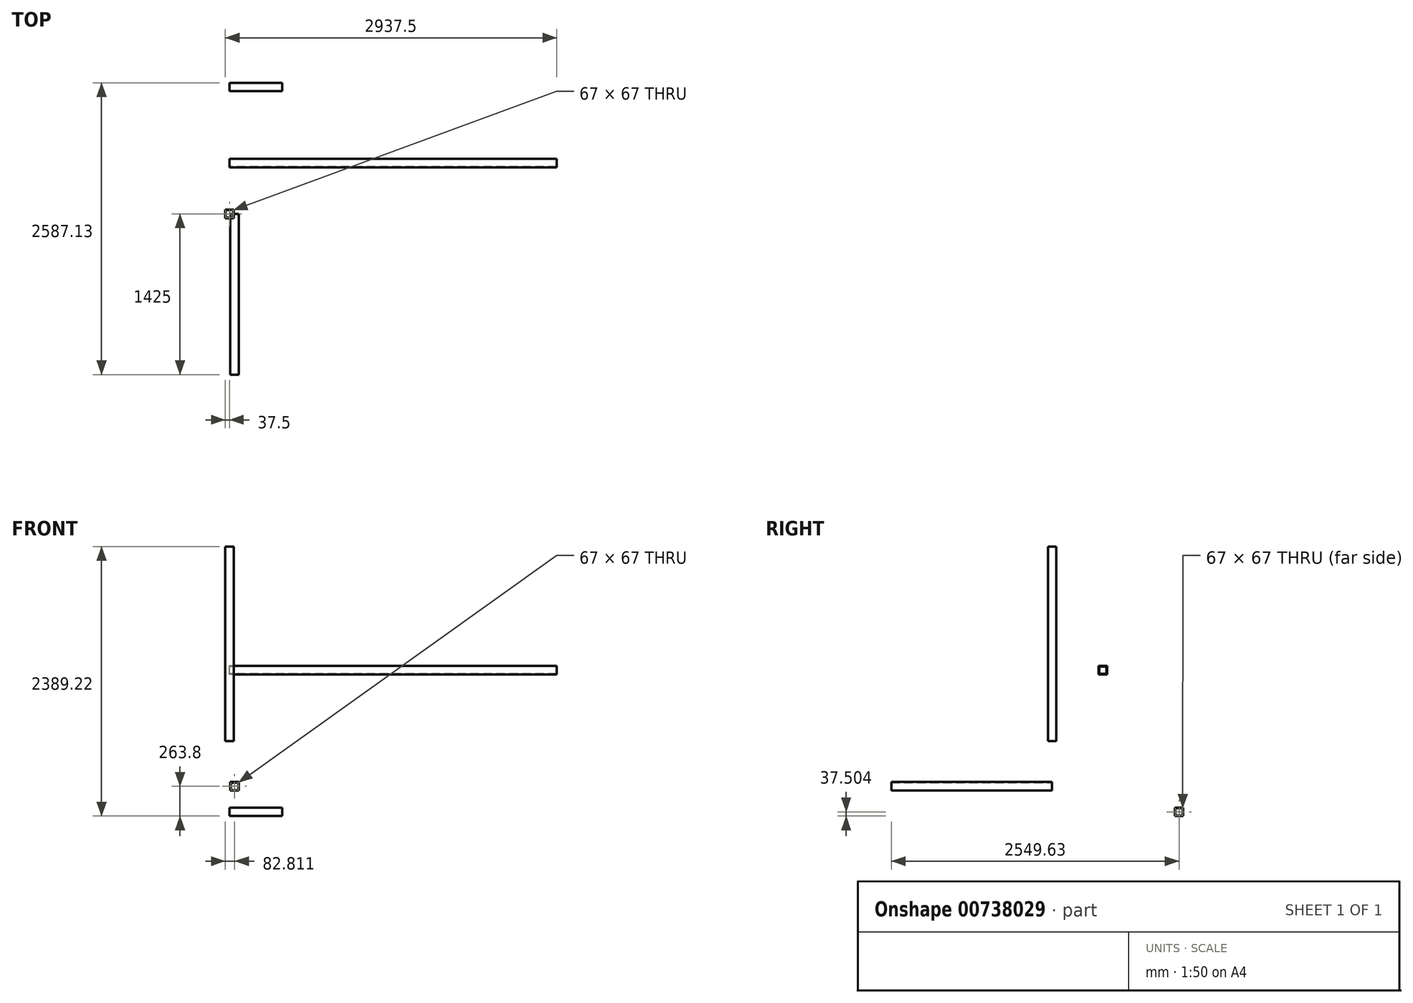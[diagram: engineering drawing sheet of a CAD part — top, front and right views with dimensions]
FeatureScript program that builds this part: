
annotation { "Feature Type Name" : "Feature", "Feature Type Description" : "" }
export const myFeature = defineFeature(function(context is Context, id is Id, definition is map)
    precondition{}
    {
        {
            var Q0;
            Q0=qCreatedBy(makeId("Top.planeOp"),FACE);
            var sketch = newSketch(context, id + "F0", { "sketchPlane" : qUnion([Q0])});
            skLineSegment(sketch, "E0.bottom", {"start": v(37.5, -37.5) * mm, "end": v(-37.5, -37.5) * mm});
            skLineSegment(sketch, "E0.top", {"start": v(37.5, 37.5) * mm, "end": v(-37.5, 37.5) * mm});
            skLineSegment(sketch, "E0.left", {"start": v(37.5, -37.5) * mm, "end": v(37.5, 37.5) * mm});
            skLineSegment(sketch, "E0.right", {"start": v(-37.5, -37.5) * mm, "end": v(-37.5, 37.5) * mm});
            skPoint(sketch, "E0.middle", {"position": v(0, 0) * mm});
            skLineSegment(sketch, "E1.0", {"start": v(33.5, 33.5) * mm, "end": v(-33.5, 33.5) * mm});
            skLineSegment(sketch, "E1.1", {"start": v(33.5, -33.5) * mm, "end": v(33.5, 33.5) * mm});
            skLineSegment(sketch, "E1.2", {"start": v(33.5, -33.5) * mm, "end": v(-33.5, -33.5) * mm});
            skLineSegment(sketch, "E1.3", {"start": v(-33.5, -33.5) * mm, "end": v(-33.5, 33.5) * mm});
            skLineSegment(sketch, "E2.bottom", {"start": v(-2581.2, 0) * mm, "end": v(-2506.2, 0) * mm});
            skLineSegment(sketch, "E2.top", {"start": v(-2581.2, -75) * mm, "end": v(-2506.2, -75) * mm});
            skLineSegment(sketch, "E2.left", {"start": v(-2581.2, 0) * mm, "end": v(-2581.2, -75) * mm});
            skLineSegment(sketch, "E2.right", {"start": v(-2506.2, 0) * mm, "end": v(-2506.2, -75) * mm});
            skPoint(sketch, "E2.middle", {"position": v(-2543.7, -37.5) * mm});
            skLineSegment(sketch, "E3.0", {"start": v(-2577.2, -4) * mm, "end": v(-2510.2, -4) * mm});
            skLineSegment(sketch, "E3.1", {"start": v(-2577.2, -4) * mm, "end": v(-2577.2, -71) * mm});
            skLineSegment(sketch, "E3.2", {"start": v(-2577.2, -71) * mm, "end": v(-2510.2, -71) * mm});
            skLineSegment(sketch, "E3.3", {"start": v(-2510.2, -4) * mm, "end": v(-2510.2, -71) * mm});
            skSolve(sketch);
        }
        {
            var Q0;
            Q0=makeQuery(id+"F0.imprint","IMPRINT",FACE,{"disambiguationData":[TD([[makeQuery(id+"F0.imprint","IMPRINT",EDGE,{"derivedFrom":sQuery(id+"F0.wireOp",EDGE,"E0.bottom")}),-1.0]])]});
            extrude(context, id + "F1", {"entities" : qUnion([Q0]), "depth" : 1725 * mm, "offsetDistance" : 25 * mm});
        }
        {
            var Q0;
            Q0=qCreatedBy(makeId("Right.planeOp"),FACE);
            var sketch = newSketch(context, id + "F2", { "sketchPlane" : qUnion([Q0])});
            skLineSegment(sketch, "E4.bottom", {"start": v(487.02, 591.17) * mm, "end": v(412.02, 591.17) * mm});
            skLineSegment(sketch, "E4.top", {"start": v(487.02, 666.17) * mm, "end": v(412.02, 666.17) * mm});
            skLineSegment(sketch, "E4.left", {"start": v(487.02, 591.17) * mm, "end": v(487.02, 666.17) * mm});
            skLineSegment(sketch, "E4.right", {"start": v(412.02, 591.17) * mm, "end": v(412.02, 666.17) * mm});
            skPoint(sketch, "E4.middle", {"position": v(449.52, 628.67) * mm});
            skLineSegment(sketch, "E5.0", {"start": v(482.02, 661.17) * mm, "end": v(417.02, 661.17) * mm});
            skLineSegment(sketch, "E5.1", {"start": v(482.02, 596.17) * mm, "end": v(482.02, 661.17) * mm});
            skLineSegment(sketch, "E5.2", {"start": v(482.02, 596.17) * mm, "end": v(417.02, 596.17) * mm});
            skLineSegment(sketch, "E5.3", {"start": v(417.02, 596.17) * mm, "end": v(417.02, 661.17) * mm});
            skSolve(sketch);
        }
        {
            var Q0;
            Q0=qSketchRegion(id+"F2",true);
            extrude(context, id + "F3", {"entities" : qUnion([Q0]), "depth" : 2900 * mm, "offsetDistance" : 25 * mm});
        }
        {
            var Q0;
            Q0=qCreatedBy(makeId("Front.planeOp"),FACE);
            var sketch = newSketch(context, id + "F4", { "sketchPlane" : qUnion([Q0])});
            skLineSegment(sketch, "E6.bottom", {"start": v(82.81, -437.92) * mm, "end": v(7.81, -437.92) * mm});
            skLineSegment(sketch, "E6.top", {"start": v(82.81, -362.92) * mm, "end": v(7.81, -362.92) * mm});
            skLineSegment(sketch, "E6.left", {"start": v(82.81, -437.92) * mm, "end": v(82.81, -362.92) * mm});
            skLineSegment(sketch, "E6.right", {"start": v(7.81, -437.92) * mm, "end": v(7.81, -362.92) * mm});
            skPoint(sketch, "E6.middle", {"position": v(45.31, -400.42) * mm});
            skLineSegment(sketch, "E7.0", {"start": v(11.81, -433.92) * mm, "end": v(11.81, -366.92) * mm});
            skLineSegment(sketch, "E7.1", {"start": v(78.81, -433.92) * mm, "end": v(11.81, -433.92) * mm});
            skLineSegment(sketch, "E7.2", {"start": v(78.81, -433.92) * mm, "end": v(78.81, -366.92) * mm});
            skLineSegment(sketch, "E7.3", {"start": v(78.81, -366.92) * mm, "end": v(11.81, -366.92) * mm});
            skSolve(sketch);
        }
        {
            var Q0;
            Q0=qSketchRegion(id+"F4",true);
            extrude(context, id + "F5", {"entities" : qUnion([Q0]), "depth" : 1425 * mm, "offsetDistance" : 25 * mm});
        }
        {
            var Q0;
            Q0=qCreatedBy(makeId("Right.planeOp"),FACE);
            var sketch = newSketch(context, id + "F6", { "sketchPlane" : qUnion([Q0])});
            skLineSegment(sketch, "E8.bottom", {"start": v(1162.13, -664.22) * mm, "end": v(1087.13, -664.22) * mm});
            skLineSegment(sketch, "E8.top", {"start": v(1162.13, -589.22) * mm, "end": v(1087.13, -589.22) * mm});
            skLineSegment(sketch, "E8.left", {"start": v(1162.13, -664.22) * mm, "end": v(1162.13, -589.22) * mm});
            skLineSegment(sketch, "E8.right", {"start": v(1087.13, -664.22) * mm, "end": v(1087.13, -589.22) * mm});
            skPoint(sketch, "E8.middle", {"position": v(1124.63, -626.72) * mm});
            skLineSegment(sketch, "E9.0", {"start": v(1091.13, -660.22) * mm, "end": v(1091.13, -593.22) * mm});
            skLineSegment(sketch, "E9.1", {"start": v(1158.13, -660.22) * mm, "end": v(1091.13, -660.22) * mm});
            skLineSegment(sketch, "E9.2", {"start": v(1158.13, -660.22) * mm, "end": v(1158.13, -593.22) * mm});
            skLineSegment(sketch, "E9.3", {"start": v(1158.13, -593.22) * mm, "end": v(1091.13, -593.22) * mm});
            skSolve(sketch);
        }
        {
            var Q0;
            Q0=qSketchRegion(id+"F6",true);
            extrude(context, id + "F7", {"entities" : qUnion([Q0]), "depth" : 466 * mm, "offsetDistance" : 25 * mm});
        }
    });
